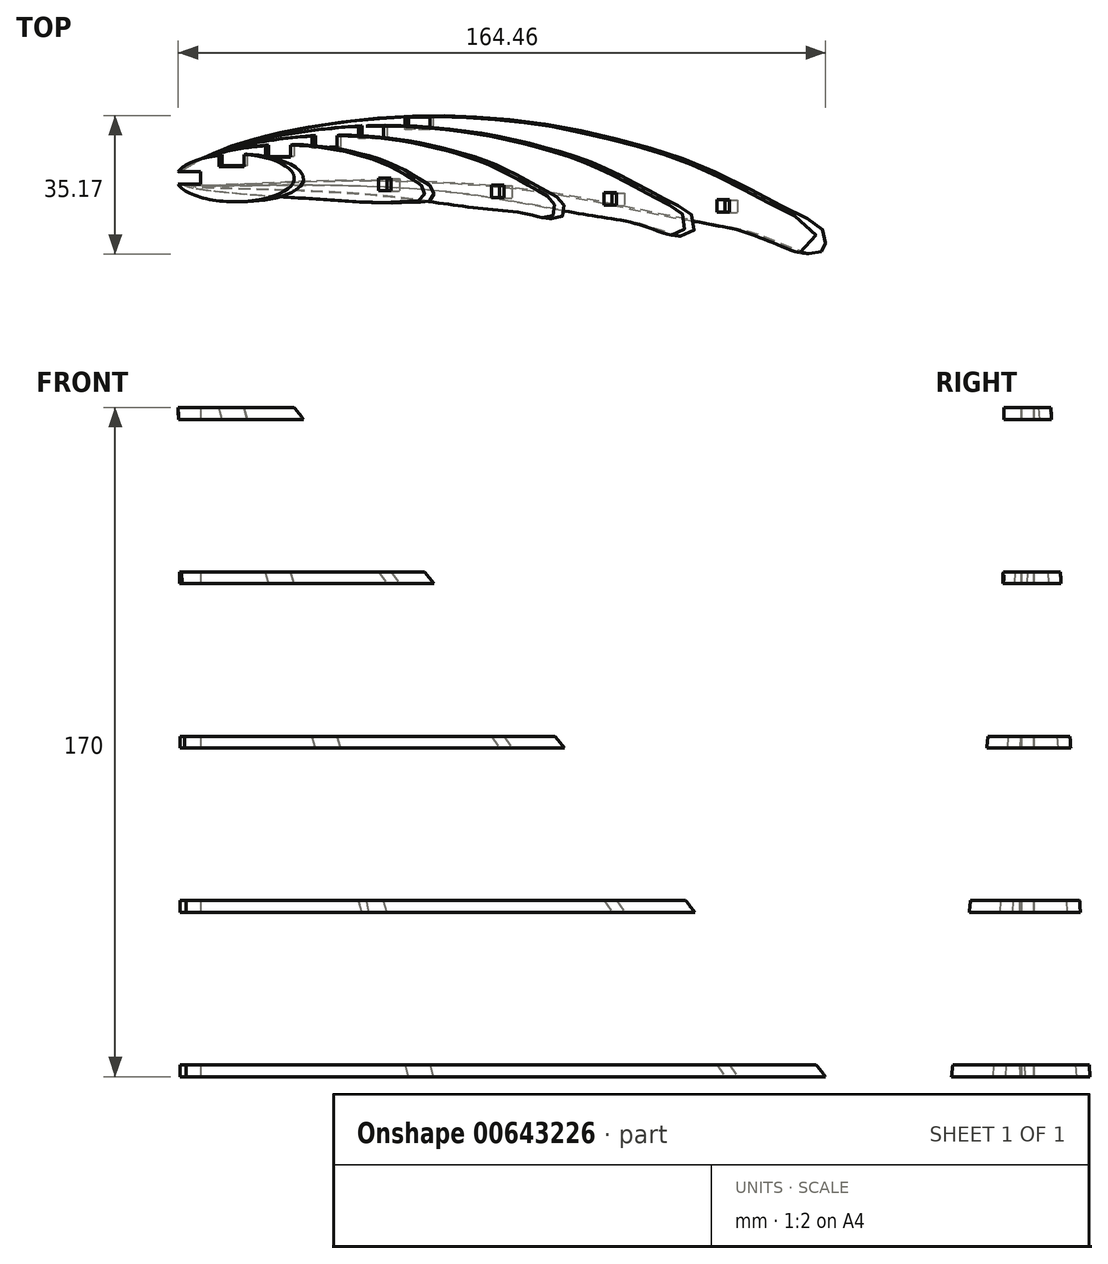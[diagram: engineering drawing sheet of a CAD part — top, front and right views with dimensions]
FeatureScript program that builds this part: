
annotation { "Feature Type Name" : "Feature", "Feature Type Description" : "" }
export const myFeature = defineFeature(function(context is Context, id is Id, definition is map)
    precondition{}
    {
        {
            var Q0;
            Q0=qCreatedBy(makeId("Top.planeOp"),FACE);
            var sketch = newSketch(context, id + "F0", { "sketchPlane" : qUnion([Q0])});
            skLineSegment(sketch, "E0", {"start": v(1, 1.71) * mm, "end": v(3.22, 2.99) * mm});
            skLineSegment(sketch, "E1", {"start": v(3.22, 2.99) * mm, "end": v(5.44, 4.24) * mm});
            skLineSegment(sketch, "E2", {"start": v(5.44, 4.24) * mm, "end": v(7.68, 5.43) * mm});
            skLineSegment(sketch, "E3", {"start": v(7.68, 5.43) * mm, "end": v(9.99, 6.53) * mm});
            skLineSegment(sketch, "E4", {"start": v(9.99, 6.53) * mm, "end": v(12.3, 7.5) * mm});
            skLineSegment(sketch, "E5", {"start": v(12.3, 7.5) * mm, "end": v(14.68, 8.38) * mm});
            skLineSegment(sketch, "E6", {"start": v(14.68, 8.38) * mm, "end": v(17.1, 9.17) * mm});
            skLineSegment(sketch, "E7", {"start": v(17.1, 9.17) * mm, "end": v(19.55, 9.87) * mm});
            skLineSegment(sketch, "E8", {"start": v(19.55, 9.87) * mm, "end": v(22.03, 10.5) * mm});
            skLineSegment(sketch, "E9", {"start": v(22.03, 10.5) * mm, "end": v(26.45, 11.52) * mm});
            skLineSegment(sketch, "E10", {"start": v(26.45, 11.52) * mm, "end": v(29.5, 12.16) * mm});
            skLineSegment(sketch, "E11", {"start": v(29.5, 12.16) * mm, "end": v(34.51, 13.11) * mm});
            skLineSegment(sketch, "E12", {"start": v(34.51, 13.11) * mm, "end": v(37.02, 13.54) * mm});
            skLineSegment(sketch, "E13", {"start": v(37.02, 13.54) * mm, "end": v(39.53, 13.94) * mm});
            skLineSegment(sketch, "E14", {"start": v(39.53, 13.94) * mm, "end": v(42.04, 14.3) * mm});
            skLineSegment(sketch, "E15", {"start": v(42.04, 14.3) * mm, "end": v(44.56, 14.62) * mm});
            skLineSegment(sketch, "E16", {"start": v(44.56, 14.62) * mm, "end": v(48.06, 15.01) * mm});
            skLineSegment(sketch, "E17", {"start": v(48.06, 15.01) * mm, "end": v(49.61, 15.16) * mm});
            skLineSegment(sketch, "E18", {"start": v(49.61, 15.16) * mm, "end": v(52.14, 15.37) * mm});
            skLineSegment(sketch, "E19", {"start": v(52.14, 15.37) * mm, "end": v(54.68, 15.53) * mm});
            skLineSegment(sketch, "E20", {"start": v(54.68, 15.53) * mm, "end": v(57.22, 15.66) * mm});
            skLineSegment(sketch, "E21", {"start": v(57.22, 15.66) * mm, "end": v(59.76, 15.76) * mm});
            skLineSegment(sketch, "E22", {"start": v(59.76, 15.76) * mm, "end": v(62.3, 15.81) * mm});
            skLineSegment(sketch, "E23", {"start": v(62.3, 15.81) * mm, "end": v(64.85, 15.83) * mm});
            skLineSegment(sketch, "E24", {"start": v(64.85, 15.83) * mm, "end": v(67.4, 15.82) * mm});
            skLineSegment(sketch, "E25", {"start": v(67.4, 15.82) * mm, "end": v(69.95, 15.77) * mm});
            skLineSegment(sketch, "E26", {"start": v(69.95, 15.77) * mm, "end": v(72.67, 15.68) * mm});
            skLineSegment(sketch, "E27", {"start": v(72.67, 15.68) * mm, "end": v(75.03, 15.57) * mm});
            skLineSegment(sketch, "E28", {"start": v(75.03, 15.57) * mm, "end": v(77.57, 15.42) * mm});
            skLineSegment(sketch, "E29", {"start": v(77.57, 15.42) * mm, "end": v(80.11, 15.23) * mm});
            skLineSegment(sketch, "E30", {"start": v(80.11, 15.23) * mm, "end": v(82.65, 15.02) * mm});
            skLineSegment(sketch, "E31", {"start": v(82.65, 15.02) * mm, "end": v(85.18, 14.77) * mm});
            skLineSegment(sketch, "E32", {"start": v(85.18, 14.77) * mm, "end": v(87.7, 14.49) * mm});
            skLineSegment(sketch, "E33", {"start": v(87.7, 14.49) * mm, "end": v(90.23, 14.17) * mm});
            skLineSegment(sketch, "E34", {"start": v(90.23, 14.17) * mm, "end": v(92.75, 13.82) * mm});
            skLineSegment(sketch, "E35", {"start": v(92.75, 13.82) * mm, "end": v(95.26, 13.44) * mm});
            skLineSegment(sketch, "E36", {"start": v(95.26, 13.44) * mm, "end": v(97.77, 13.02) * mm});
            skLineSegment(sketch, "E37", {"start": v(97.77, 13.02) * mm, "end": v(100.27, 12.56) * mm});
            skLineSegment(sketch, "E38", {"start": v(100.27, 12.56) * mm, "end": v(102.77, 12.08) * mm});
            skLineSegment(sketch, "E39", {"start": v(102.77, 12.08) * mm, "end": v(105.26, 11.56) * mm});
            skLineSegment(sketch, "E40", {"start": v(105.26, 11.56) * mm, "end": v(107.74, 11) * mm});
            skLineSegment(sketch, "E41", {"start": v(107.74, 11) * mm, "end": v(110.22, 10.41) * mm});
            skLineSegment(sketch, "E42", {"start": v(110.22, 10.41) * mm, "end": v(112.68, 9.79) * mm});
            skLineSegment(sketch, "E43", {"start": v(112.68, 9.79) * mm, "end": v(115.14, 9.13) * mm});
            skLineSegment(sketch, "E44", {"start": v(115.14, 9.13) * mm, "end": v(117.6, 8.44) * mm});
            skLineSegment(sketch, "E45", {"start": v(117.6, 8.44) * mm, "end": v(120.03, 7.72) * mm});
            skLineSegment(sketch, "E46", {"start": v(120.03, 7.72) * mm, "end": v(121.72, 7.2) * mm});
            skLineSegment(sketch, "E47", {"start": v(121.72, 7.2) * mm, "end": v(124.88, 6.17) * mm});
            skLineSegment(sketch, "E48", {"start": v(124.88, 6.17) * mm, "end": v(127.29, 5.34) * mm});
            skLineSegment(sketch, "E49", {"start": v(127.29, 5.34) * mm, "end": v(129.68, 4.48) * mm});
            skLineSegment(sketch, "E50", {"start": v(129.68, 4.48) * mm, "end": v(132.06, 3.58) * mm});
            skLineSegment(sketch, "E51", {"start": v(132.06, 3.58) * mm, "end": v(134.43, 2.64) * mm});
            skLineSegment(sketch, "E52", {"start": v(134.43, 2.64) * mm, "end": v(136.78, 1.66) * mm});
            skLineSegment(sketch, "E53", {"start": v(136.78, 1.66) * mm, "end": v(139.1, 0.64) * mm});
            skLineSegment(sketch, "E54", {"start": v(139.1, 0.64) * mm, "end": v(142.17, -0.78) * mm});
            skLineSegment(sketch, "E55", {"start": v(142.17, -0.78) * mm, "end": v(143.7, -1.53) * mm});
            skLineSegment(sketch, "E56", {"start": v(143.7, -1.53) * mm, "end": v(145.97, -2.68) * mm});
            skLineSegment(sketch, "E57", {"start": v(145.97, -2.68) * mm, "end": v(148.22, -3.85) * mm});
            skLineSegment(sketch, "E58", {"start": v(148.22, -3.85) * mm, "end": v(152.69, -6.28) * mm});
            skLineSegment(sketch, "E59", {"start": v(152.69, -6.28) * mm, "end": v(157.13, -8.76) * mm});
            skLineSegment(sketch, "E60", {"start": v(1, 1.71) * mm, "end": v(0.87, 1.54) * mm});
            skLineSegment(sketch, "E61", {"start": v(0.87, 1.54) * mm, "end": v(0.73, 1.38) * mm});
            skLineSegment(sketch, "E62", {"start": v(0.73, 1.38) * mm, "end": v(0.6, 1.21) * mm});
            skLineSegment(sketch, "E63", {"start": v(0.6, 1.21) * mm, "end": v(0.48, 1.05) * mm});
            skLineSegment(sketch, "E64", {"start": v(0.48, 1.05) * mm, "end": v(0.42, 0.97) * mm});
            skLineSegment(sketch, "E65", {"start": v(0.42, 0.97) * mm, "end": v(0.37, 0.9) * mm});
            skLineSegment(sketch, "E66", {"start": v(0.37, 0.9) * mm, "end": v(0.33, 0.84) * mm});
            skLineSegment(sketch, "E67", {"start": v(0.33, 0.84) * mm, "end": v(0.27, 0.74) * mm});
            skLineSegment(sketch, "E68", {"start": v(0.27, 0.74) * mm, "end": v(0.23, 0.67) * mm});
            skLineSegment(sketch, "E69", {"start": v(0.23, 0.67) * mm, "end": v(0.19, 0.6) * mm});
            skLineSegment(sketch, "E70", {"start": v(0.19, 0.6) * mm, "end": v(0.15, 0.52) * mm});
            skLineSegment(sketch, "E71", {"start": v(0.15, 0.52) * mm, "end": v(0.12, 0.45) * mm});
            skLineSegment(sketch, "E72", {"start": v(0.12, 0.45) * mm, "end": v(0.1, 0.38) * mm});
            skLineSegment(sketch, "E73", {"start": v(0.1, 0.38) * mm, "end": v(0.07, 0.32) * mm});
            skLineSegment(sketch, "E74", {"start": v(0.07, 0.32) * mm, "end": v(0.05, 0.25) * mm});
            skLineSegment(sketch, "E75", {"start": v(0.05, 0.25) * mm, "end": v(0.03, 0.19) * mm});
            skLineSegment(sketch, "E76", {"start": v(0.03, 0.19) * mm, "end": v(0.02, 0.12) * mm});
            skLineSegment(sketch, "E77", {"start": v(0.02, 0.12) * mm, "end": v(0, 0.06) * mm});
            skLineSegment(sketch, "E78", {"start": v(0, 0.06) * mm, "end": v(0, 0) * mm});
            skLineSegment(sketch, "E79", {"start": v(0, 0) * mm, "end": v(0, -0.06) * mm});
            skLineSegment(sketch, "E80", {"start": v(0, -0.06) * mm, "end": v(0, -0.12) * mm});
            skLineSegment(sketch, "E81", {"start": v(0, -0.12) * mm, "end": v(0, -0.18) * mm});
            skLineSegment(sketch, "E82", {"start": v(0, -0.18) * mm, "end": v(0, -0.23) * mm});
            skLineSegment(sketch, "E83", {"start": v(0, -0.23) * mm, "end": v(0.02, -0.29) * mm});
            skLineSegment(sketch, "E84", {"start": v(0.02, -0.29) * mm, "end": v(0.03, -0.34) * mm});
            skLineSegment(sketch, "E85", {"start": v(0.03, -0.34) * mm, "end": v(0.05, -0.4) * mm});
            skLineSegment(sketch, "E86", {"start": v(0.05, -0.4) * mm, "end": v(0.07, -0.44) * mm});
            skLineSegment(sketch, "E87", {"start": v(0.07, -0.44) * mm, "end": v(0.1, -0.5) * mm});
            skLineSegment(sketch, "E88", {"start": v(0.1, -0.5) * mm, "end": v(0.12, -0.54) * mm});
            skLineSegment(sketch, "E89", {"start": v(0.12, -0.54) * mm, "end": v(0.15, -0.6) * mm});
            skLineSegment(sketch, "E90", {"start": v(0.15, -0.6) * mm, "end": v(0.18, -0.64) * mm});
            skLineSegment(sketch, "E91", {"start": v(0.18, -0.64) * mm, "end": v(0.22, -0.68) * mm});
            skLineSegment(sketch, "E92", {"start": v(0.22, -0.68) * mm, "end": v(0.25, -0.73) * mm});
            skLineSegment(sketch, "E93", {"start": v(0.25, -0.73) * mm, "end": v(0.3, -0.77) * mm});
            skLineSegment(sketch, "E94", {"start": v(0.3, -0.77) * mm, "end": v(0.34, -0.81) * mm});
            skLineSegment(sketch, "E95", {"start": v(0.34, -0.81) * mm, "end": v(0.39, -0.86) * mm});
            skLineSegment(sketch, "E96", {"start": v(0.39, -0.86) * mm, "end": v(0.44, -0.9) * mm});
            skLineSegment(sketch, "E97", {"start": v(0.44, -0.9) * mm, "end": v(0.5, -0.94) * mm});
            skLineSegment(sketch, "E98", {"start": v(0.5, -0.94) * mm, "end": v(0.6, -1.01) * mm});
            skLineSegment(sketch, "E99", {"start": v(0.6, -1.01) * mm, "end": v(0.73, -1.08) * mm});
            skLineSegment(sketch, "E100", {"start": v(0.73, -1.08) * mm, "end": v(0.87, -1.15) * mm});
            skLineSegment(sketch, "E101", {"start": v(0.87, -1.15) * mm, "end": v(1.02, -1.22) * mm});
            skLineSegment(sketch, "E102", {"start": v(1.02, -1.22) * mm, "end": v(1.17, -1.28) * mm});
            skLineSegment(sketch, "E103", {"start": v(1.17, -1.28) * mm, "end": v(1.34, -1.33) * mm});
            skLineSegment(sketch, "E104", {"start": v(1.34, -1.33) * mm, "end": v(1.52, -1.39) * mm});
            skLineSegment(sketch, "E105", {"start": v(1.52, -1.39) * mm, "end": v(1.7, -1.44) * mm});
            skLineSegment(sketch, "E106", {"start": v(1.7, -1.44) * mm, "end": v(1.9, -1.48) * mm});
            skLineSegment(sketch, "E107", {"start": v(1.9, -1.48) * mm, "end": v(2.1, -1.53) * mm});
            skLineSegment(sketch, "E108", {"start": v(2.1, -1.53) * mm, "end": v(2.32, -1.57) * mm});
            skLineSegment(sketch, "E109", {"start": v(2.32, -1.57) * mm, "end": v(2.54, -1.6) * mm});
            skLineSegment(sketch, "E110", {"start": v(2.54, -1.6) * mm, "end": v(2.77, -1.64) * mm});
            skLineSegment(sketch, "E111", {"start": v(2.77, -1.64) * mm, "end": v(3, -1.67) * mm});
            skLineSegment(sketch, "E112", {"start": v(3, -1.67) * mm, "end": v(3.25, -1.7) * mm});
            skLineSegment(sketch, "E113", {"start": v(3.25, -1.7) * mm, "end": v(3.5, -1.73) * mm});
            skLineSegment(sketch, "E114", {"start": v(3.5, -1.73) * mm, "end": v(3.77, -1.75) * mm});
            skLineSegment(sketch, "E115", {"start": v(3.77, -1.75) * mm, "end": v(4.03, -1.77) * mm});
            skLineSegment(sketch, "E116", {"start": v(4.03, -1.77) * mm, "end": v(4.3, -1.8) * mm});
            skLineSegment(sketch, "E117", {"start": v(4.3, -1.8) * mm, "end": v(4.59, -1.8) * mm});
            skLineSegment(sketch, "E118", {"start": v(4.59, -1.8) * mm, "end": v(4.87, -1.82) * mm});
            skLineSegment(sketch, "E119", {"start": v(4.87, -1.82) * mm, "end": v(5.16, -1.83) * mm});
            skLineSegment(sketch, "E120", {"start": v(5.16, -1.83) * mm, "end": v(5.46, -1.84) * mm});
            skLineSegment(sketch, "E121", {"start": v(5.46, -1.84) * mm, "end": v(5.76, -1.85) * mm});
            skLineSegment(sketch, "E122", {"start": v(5.76, -1.85) * mm, "end": v(6.07, -1.86) * mm});
            skLineSegment(sketch, "E123", {"start": v(6.07, -1.86) * mm, "end": v(6.38, -1.86) * mm});
            skLineSegment(sketch, "E124", {"start": v(6.38, -1.86) * mm, "end": v(6.7, -1.87) * mm});
            skLineSegment(sketch, "E125", {"start": v(6.7, -1.87) * mm, "end": v(7.02, -1.87) * mm});
            skLineSegment(sketch, "E126", {"start": v(7.02, -1.87) * mm, "end": v(7.34, -1.87) * mm});
            skLineSegment(sketch, "E127", {"start": v(7.34, -1.87) * mm, "end": v(7.67, -1.87) * mm});
            skLineSegment(sketch, "E128", {"start": v(7.67, -1.87) * mm, "end": v(8, -1.87) * mm});
            skLineSegment(sketch, "E129", {"start": v(8, -1.87) * mm, "end": v(8.34, -1.86) * mm});
            skLineSegment(sketch, "E130", {"start": v(8.34, -1.86) * mm, "end": v(8.67, -1.86) * mm});
            skLineSegment(sketch, "E131", {"start": v(8.67, -1.86) * mm, "end": v(9.36, -1.85) * mm});
            skLineSegment(sketch, "E132", {"start": v(9.36, -1.85) * mm, "end": v(10.05, -1.83) * mm});
            skLineSegment(sketch, "E133", {"start": v(10.05, -1.83) * mm, "end": v(10.74, -1.82) * mm});
            skLineSegment(sketch, "E134", {"start": v(10.74, -1.82) * mm, "end": v(12.15, -1.78) * mm});
            skLineSegment(sketch, "E135", {"start": v(157.13, -8.76) * mm, "end": v(159.65, -9.9) * mm});
            skLineSegment(sketch, "E136", {"start": v(159.65, -9.9) * mm, "end": v(162.12, -11.02) * mm});
            skLineSegment(sketch, "E137", {"start": v(162.12, -11.02) * mm, "end": v(163.97, -12.8) * mm});
            skLineSegment(sketch, "E138", {"start": v(163.97, -12.8) * mm, "end": v(165.18, -13.97) * mm});
            skLineSegment(sketch, "E139", {"start": v(165.18, -13.97) * mm, "end": v(165.11, -15.41) * mm});
            skLineSegment(sketch, "E140", {"start": v(165.11, -15.41) * mm, "end": v(164.85, -16.72) * mm});
            skLineSegment(sketch, "E141", {"start": v(164.85, -16.72) * mm, "end": v(164.68, -17.32) * mm});
            skLineSegment(sketch, "E142", {"start": v(164.68, -17.32) * mm, "end": v(164.48, -17.86) * mm});
            skLineSegment(sketch, "E143", {"start": v(164.48, -17.86) * mm, "end": v(164.28, -18.24) * mm});
            skLineSegment(sketch, "E144", {"start": v(164.28, -18.24) * mm, "end": v(163.92, -18.7) * mm});
            skLineSegment(sketch, "E145", {"start": v(163.92, -18.7) * mm, "end": v(163.55, -18.98) * mm});
            skLineSegment(sketch, "E146", {"start": v(163.55, -18.98) * mm, "end": v(163.13, -19.18) * mm});
            skLineSegment(sketch, "E147", {"start": v(163.13, -19.18) * mm, "end": v(162.66, -19.3) * mm});
            skLineSegment(sketch, "E148", {"start": v(162.66, -19.3) * mm, "end": v(162.15, -19.36) * mm});
            skLineSegment(sketch, "E149", {"start": v(162.15, -19.36) * mm, "end": v(161.6, -19.35) * mm});
            skLineSegment(sketch, "E150", {"start": v(161.6, -19.35) * mm, "end": v(161, -19.28) * mm});
            skLineSegment(sketch, "E151", {"start": v(161, -19.28) * mm, "end": v(160.39, -19.16) * mm});
            skLineSegment(sketch, "E152", {"start": v(160.39, -19.16) * mm, "end": v(159.74, -19) * mm});
            skLineSegment(sketch, "E153", {"start": v(159.74, -19) * mm, "end": v(159.07, -18.79) * mm});
            skLineSegment(sketch, "E154", {"start": v(159.07, -18.79) * mm, "end": v(158.37, -18.54) * mm});
            skLineSegment(sketch, "E155", {"start": v(158.37, -18.54) * mm, "end": v(156.94, -17.98) * mm});
            skLineSegment(sketch, "E156", {"start": v(156.94, -17.98) * mm, "end": v(155.48, -17.36) * mm});
            skLineSegment(sketch, "E157", {"start": v(155.48, -17.36) * mm, "end": v(153.3, -16.41) * mm});
            skLineSegment(sketch, "E158", {"start": v(153.3, -16.41) * mm, "end": v(152.58, -16.1) * mm});
            skLineSegment(sketch, "E159", {"start": v(152.58, -16.1) * mm, "end": v(151.19, -15.54) * mm});
            skLineSegment(sketch, "E160", {"start": v(151.19, -15.54) * mm, "end": v(149.84, -15.03) * mm});
            skLineSegment(sketch, "E161", {"start": v(149.84, -15.03) * mm, "end": v(148.53, -14.57) * mm});
            skLineSegment(sketch, "E162", {"start": v(148.53, -14.57) * mm, "end": v(147.26, -14.14) * mm});
            skLineSegment(sketch, "E163", {"start": v(147.26, -14.14) * mm, "end": v(146.02, -13.76) * mm});
            skLineSegment(sketch, "E164", {"start": v(146.02, -13.76) * mm, "end": v(144.8, -13.4) * mm});
            skLineSegment(sketch, "E165", {"start": v(144.8, -13.4) * mm, "end": v(143.62, -13.09) * mm});
            skLineSegment(sketch, "E166", {"start": v(143.62, -13.09) * mm, "end": v(142.46, -12.8) * mm});
            skLineSegment(sketch, "E167", {"start": v(142.46, -12.8) * mm, "end": v(140.2, -12.3) * mm});
            skLineSegment(sketch, "E168", {"start": v(140.2, -12.3) * mm, "end": v(137.98, -11.85) * mm});
            skLineSegment(sketch, "E169", {"start": v(137.98, -11.85) * mm, "end": v(133.6, -11.09) * mm});
            skLineSegment(sketch, "E170", {"start": v(133.6, -11.09) * mm, "end": v(131.7, -10.76) * mm});
            skLineSegment(sketch, "E171", {"start": v(131.7, -10.76) * mm, "end": v(129.14, -10.3) * mm});
            skLineSegment(sketch, "E172", {"start": v(129.14, -10.3) * mm, "end": v(126.85, -9.85) * mm});
            skLineSegment(sketch, "E173", {"start": v(126.85, -9.85) * mm, "end": v(124.52, -9.39) * mm});
            skLineSegment(sketch, "E174", {"start": v(124.52, -9.39) * mm, "end": v(122.15, -8.9) * mm});
            skLineSegment(sketch, "E175", {"start": v(122.15, -8.9) * mm, "end": v(119.76, -8.4) * mm});
            skLineSegment(sketch, "E176", {"start": v(119.76, -8.4) * mm, "end": v(114.91, -7.38) * mm});
            skLineSegment(sketch, "E177", {"start": v(114.91, -7.38) * mm, "end": v(110, -6.37) * mm});
            skLineSegment(sketch, "E178", {"start": v(110, -6.37) * mm, "end": v(105.06, -5.4) * mm});
            skLineSegment(sketch, "E179", {"start": v(105.06, -5.4) * mm, "end": v(100.77, -4.6) * mm});
            skLineSegment(sketch, "E180", {"start": v(100.77, -4.6) * mm, "end": v(95.2, -3.7) * mm});
            skLineSegment(sketch, "E181", {"start": v(95.2, -3.7) * mm, "end": v(90.32, -3.02) * mm});
            skLineSegment(sketch, "E182", {"start": v(90.32, -3.02) * mm, "end": v(85.45, -2.43) * mm});
            skLineSegment(sketch, "E183", {"start": v(85.45, -2.43) * mm, "end": v(80.6, -1.94) * mm});
            skLineSegment(sketch, "E184", {"start": v(80.6, -1.94) * mm, "end": v(75.74, -1.53) * mm});
            skLineSegment(sketch, "E185", {"start": v(75.74, -1.53) * mm, "end": v(70.88, -1.2) * mm});
            skLineSegment(sketch, "E186", {"start": v(70.88, -1.2) * mm, "end": v(66.02, -0.95) * mm});
            skLineSegment(sketch, "E187", {"start": v(66.02, -0.95) * mm, "end": v(61.14, -0.76) * mm});
            skLineSegment(sketch, "E188", {"start": v(61.14, -0.76) * mm, "end": v(56.25, -0.64) * mm});
            skLineSegment(sketch, "E189", {"start": v(56.25, -0.64) * mm, "end": v(51.35, -0.58) * mm});
            skLineSegment(sketch, "E190", {"start": v(51.35, -0.58) * mm, "end": v(46.44, -0.58) * mm});
            skLineSegment(sketch, "E191", {"start": v(46.44, -0.58) * mm, "end": v(41.53, -0.63) * mm});
            skLineSegment(sketch, "E192", {"start": v(41.53, -0.63) * mm, "end": v(34.6, -0.78) * mm});
            skLineSegment(sketch, "E193", {"start": v(34.6, -0.78) * mm, "end": v(31.72, -0.88) * mm});
            skLineSegment(sketch, "E194", {"start": v(31.72, -0.88) * mm, "end": v(21.93, -1.29) * mm});
            skLineSegment(sketch, "E195", {"start": v(21.93, -1.29) * mm, "end": v(12.15, -1.78) * mm});
            skSolve(sketch);
        }
        {
            var Q0;
            Q0=qCreatedBy(makeId("Top.planeOp"),FACE);
            var sketch = newSketch(context, id + "F1", { "sketchPlane" : qUnion([Q0])});
            skPoint(sketch, "E196.0", {"position": v(0, 0) * mm});
            skPoint(sketch, "E196.1", {"position": v(0.1, 0.38) * mm});
            skPoint(sketch, "E196.2", {"position": v(0.33, 0.84) * mm});
            skPoint(sketch, "E196.3", {"position": v(0.73, 1.38) * mm});
            skPoint(sketch, "E196.4", {"position": v(5.44, 4.24) * mm});
            skPoint(sketch, "E196.5", {"position": v(12.3, 7.5) * mm});
            skPoint(sketch, "E196.6", {"position": v(22.03, 10.5) * mm});
            skPoint(sketch, "E196.7", {"position": v(57.22, 15.66) * mm});
            skPoint(sketch, "E196.8", {"position": v(75.03, 15.57) * mm});
            skPoint(sketch, "E196.9", {"position": v(95.26, 13.44) * mm});
            skPoint(sketch, "E196.10", {"position": v(117.6, 8.44) * mm});
            skPoint(sketch, "E196.11", {"position": v(136.78, 1.66) * mm});
            skPoint(sketch, "E196.12", {"position": v(157.13, -8.76) * mm});
            skPoint(sketch, "E196.13", {"position": v(163.97, -12.8) * mm});
            skPoint(sketch, "E196.14", {"position": v(164.48, -17.86) * mm});
            skPoint(sketch, "E196.15", {"position": v(163.55, -18.98) * mm});
            skPoint(sketch, "E196.16", {"position": v(160.39, -19.16) * mm});
            skPoint(sketch, "E196.17", {"position": v(155.48, -17.36) * mm});
            skPoint(sketch, "E196.18", {"position": v(148.53, -14.57) * mm});
            skPoint(sketch, "E196.19", {"position": v(143.62, -13.09) * mm});
            skPoint(sketch, "E196.20", {"position": v(105.06, -5.4) * mm});
            skPoint(sketch, "E196.21", {"position": v(80.6, -1.94) * mm});
            skPoint(sketch, "E196.22", {"position": v(51.35, -0.58) * mm});
            skPoint(sketch, "E196.23", {"position": v(21.93, -1.29) * mm});
            skPoint(sketch, "E196.24", {"position": v(9.36, -1.85) * mm});
            skPoint(sketch, "E196.25", {"position": v(5.46, -1.84) * mm});
            skPoint(sketch, "E196.26", {"position": v(3, -1.67) * mm});
            skPoint(sketch, "E196.27", {"position": v(0.39, -0.86) * mm});
            skPoint(sketch, "E196.28", {"position": v(0.1, -0.5) * mm});
            skPoint(sketch, "E196.29", {"position": v(35.77, 13.33) * mm});
            skPoint(sketch, "E196.30", {"position": v(164.98, -16.07) * mm});
            skPoint(sketch, "E196.31", {"position": v(125.68, -9.62) * mm});
            skPoint(sketch, "E196.32", {"position": v(38.06, -0.7) * mm});
            skFitSpline(sketch, "E197", {"points": [v(0, 0) * mm, v(0.1, 0.38) * mm, v(0.33, 0.84) * mm, v(0.73, 1.38) * mm, v(5.44, 4.24) * mm, v(12.3, 7.5) * mm, v(22.03, 10.5) * mm, v(35.77, 13.33) * mm, v(57.22, 15.66) * mm, v(75.03, 15.57) * mm, v(95.26, 13.44) * mm, v(117.6, 8.44) * mm, v(136.78, 1.66) * mm, v(157.13, -8.76) * mm, v(163.97, -12.8) * mm, v(164.98, -16.07) * mm, v(164.48, -17.86) * mm, v(163.55, -18.98) * mm, v(160.39, -19.16) * mm, v(155.48, -17.36) * mm, v(148.53, -14.57) * mm, v(143.62, -13.09) * mm, v(125.68, -9.62) * mm, v(105.06, -5.4) * mm, v(80.6, -1.94) * mm, v(51.35, -0.58) * mm, v(38.06, -0.7) * mm, v(21.93, -1.29) * mm, v(9.36, -1.85) * mm, v(5.46, -1.84) * mm, v(3, -1.67) * mm, v(0.39, -0.86) * mm, v(0.1, -0.5) * mm, v(0, 0) * mm]});
            skSolve(sketch);
        }
        {
            var Q0;
            Q0=qCreatedBy(makeId("Top.planeOp"),FACE);
            cPlane(context, id + "F2", {"entities" : qUnion([Q0]), "cplaneType" : CPlaneType.OFFSET, "offset" : 170 * mm, "width" : 150 * mm, "height" : 150 * mm});
        }
        {
            var Q0;
            Q0=qCreatedBy(id+"F2.planeOp",FACE);
            var sketch = newSketch(context, id + "F3", { "sketchPlane" : qUnion([Q0])});
            skEllipse(sketch, "E198", {"center": v(15, 0) * mm, "majorRadius": 15 * mm, "minorRadius": 6.01 * mm, "majorAxis": v(-1, 0)});
            skSolve(sketch);
        }
        {
            var Q0;
            Q0=makeQuery(id+"F1.imprint","IMPRINT",FACE,{"disambiguationData":[TD([[makeQuery(id+"F1.imprint","IMPRINT",EDGE,{"derivedFrom":sQuery(id+"F1.wireOp",EDGE,"E197")}),-1.0]])]});
            var Q1;
            Q1=makeQuery(id+"F3.imprint","IMPRINT",FACE,{"disambiguationData":[TD([[makeQuery(id+"F3.imprint","IMPRINT",EDGE,{"derivedFrom":sQuery(id+"F3.wireOp",EDGE,"E198")}),1.0]])]});
            loft(context, id + "F4", {"sheetProfilesArray" : [{ "sheetProfileEntities" : qUnion([Q0]) }, { "sheetProfileEntities" : qUnion([Q1]) }]});
        }
        {
            var Q0;
            Q0=qCreatedBy(makeId("Front.planeOp"),FACE);
            var sketch = newSketch(context, id + "F5", { "sketchPlane" : qUnion([Q0])});
            skLineSegment(sketch, "E199", {"start": v(0, 0) * mm, "end": v(0, 3) * mm, "construction": true});
            skLineSegment(sketch, "E200.bottom", {"start": v(0, 3) * mm, "end": v(214.07, 3) * mm});
            skLineSegment(sketch, "E200.top", {"start": v(0, 41.75) * mm, "end": v(214.07, 41.75) * mm});
            skLineSegment(sketch, "E200.left", {"start": v(0, 3) * mm, "end": v(0, 41.75) * mm});
            skLineSegment(sketch, "E200.right", {"start": v(214.07, 3) * mm, "end": v(214.07, 41.75) * mm});
            skLineSegment(sketch, "E201", {"start": v(0, 41.75) * mm, "end": v(0, 44.75) * mm, "construction": true});
            skLineSegment(sketch, "E202.0.1.0", {"start": v(0, 83.5) * mm, "end": v(214.07, 83.5) * mm});
            skLineSegment(sketch, "E202.0.1.1", {"start": v(0, 44.75) * mm, "end": v(0, 83.5) * mm});
            skLineSegment(sketch, "E202.0.1.2", {"start": v(214.07, 44.75) * mm, "end": v(214.07, 83.5) * mm});
            skLineSegment(sketch, "E202.0.1.3", {"start": v(0, 44.75) * mm, "end": v(214.07, 44.75) * mm});
            skLineSegment(sketch, "E202.0.1.4", {"start": v(0, 83.5) * mm, "end": v(0, 86.5) * mm, "construction": true});
            skLineSegment(sketch, "E202.0.2.0", {"start": v(0, 125.25) * mm, "end": v(214.07, 125.25) * mm});
            skLineSegment(sketch, "E202.0.2.1", {"start": v(0, 86.5) * mm, "end": v(0, 125.25) * mm});
            skLineSegment(sketch, "E202.0.2.2", {"start": v(214.07, 86.5) * mm, "end": v(214.07, 125.25) * mm});
            skLineSegment(sketch, "E202.0.2.3", {"start": v(0, 86.5) * mm, "end": v(214.07, 86.5) * mm});
            skLineSegment(sketch, "E202.0.2.4", {"start": v(0, 125.25) * mm, "end": v(0, 128.25) * mm, "construction": true});
            skLineSegment(sketch, "E202.0.2.5", {"start": v(0, 83.5) * mm, "end": v(0, 86.5) * mm, "construction": true});
            skLineSegment(sketch, "E202.0.3.0", {"start": v(0, 167) * mm, "end": v(214.07, 167) * mm});
            skLineSegment(sketch, "E202.0.3.1", {"start": v(0, 128.25) * mm, "end": v(0, 167) * mm});
            skLineSegment(sketch, "E202.0.3.2", {"start": v(214.07, 128.25) * mm, "end": v(214.07, 167) * mm});
            skLineSegment(sketch, "E202.0.3.3", {"start": v(0, 128.25) * mm, "end": v(214.07, 128.25) * mm});
            skLineSegment(sketch, "E202.0.3.4", {"start": v(0, 167) * mm, "end": v(0, 170) * mm, "construction": true});
            skLineSegment(sketch, "E202.0.3.5", {"start": v(0, 125.25) * mm, "end": v(0, 128.25) * mm, "construction": true});
            skLineSegment(sketch, "E202.direction1", {"start": v(0, 0) * mm, "end": v(25, 0) * mm, "construction": true});
            skLineSegment(sketch, "E202.direction2", {"start": v(0, 0) * mm, "end": v(0, 41.75) * mm, "construction": true});
            skSolve(sketch);
        }
        {
            var Q0;
            Q0 = qSketchRegion(id + "F5", true);
            extrude(context, id + "F6", {"entities" : qUnion([Q0]), "operationType" : NewBodyOperationType.REMOVE, "oppositeDirection" : true, "depth" : 25 * mm, "offsetDistance" : 25 * mm});
        }
        {
            var Q0;
            Q0 = qSketchRegion(id + "F5", true);
            extrude(context, id + "F7", {"entities" : qUnion([Q0]), "operationType" : NewBodyOperationType.REMOVE, "depth" : 25 * mm, "offsetDistance" : 25 * mm});
        }
        {
            var Q0;
            Q0=qCreatedBy(makeId("Top.planeOp"),FACE);
            var sketch = newSketch(context, id + "F8", { "sketchPlane" : qUnion([Q0])});
            skLineSegment(sketch, "E203", {"start": v(0, 0) * mm, "end": v(3, 0) * mm, "construction": true});
            skLineSegment(sketch, "E204.bottom", {"start": v(6.17, -1.59) * mm, "end": v(-0.17, -1.59) * mm});
            skLineSegment(sketch, "E204.top", {"start": v(6.17, 1.59) * mm, "end": v(-0.17, 1.59) * mm});
            skLineSegment(sketch, "E204.left", {"start": v(6.17, -1.59) * mm, "end": v(6.17, 1.59) * mm});
            skLineSegment(sketch, "E204.right", {"start": v(-0.17, -1.59) * mm, "end": v(-0.18, 1.59) * mm});
            skPoint(sketch, "E204.middle", {"position": v(3, 0) * mm});
            skSolve(sketch);
        }
        {
            var Q0;
            Q0=makeQuery(id+"F8.imprint","IMPRINT",FACE,{"disambiguationData":[TD([[makeQuery(id+"F8.imprint","IMPRINT",EDGE,{"derivedFrom":sQuery(id+"F8.wireOp",EDGE,"E204.bottom")}),-1.0]])]});
            extrude(context, id + "F9", {"entities" : qUnion([Q0]), "operationType" : NewBodyOperationType.REMOVE, "depth" : 204.2 * mm, "offsetDistance" : 25 * mm});
        }
        {
            var Q0;
            Q0=qCreatedBy(makeId("Top.planeOp"),FACE);
            var sketch = newSketch(context, id + "F10", { "sketchPlane" : qUnion([Q0])});
            skPoint(sketch, "E205", {"position": v(62.22, 15.71) * mm});
            skLineSegment(sketch, "E206", {"start": v(62.22, 15.71) * mm, "end": v(62.22, 12.5) * mm, "construction": true});
            skLineSegment(sketch, "E207", {"start": v(62.22, 12.5) * mm, "end": v(59.05, 12.5) * mm});
            skLineSegment(sketch, "E208", {"start": v(62.22, 12.5) * mm, "end": v(65.4, 12.5) * mm});
            skLineSegment(sketch, "E209", {"start": v(65.4, 12.5) * mm, "end": v(65.4, 15.71) * mm});
            skLineSegment(sketch, "E210", {"start": v(65.4, 15.71) * mm, "end": v(59.05, 15.71) * mm});
            skLineSegment(sketch, "E211", {"start": v(59.05, 15.71) * mm, "end": v(59.05, 12.5) * mm});
            skPoint(sketch, "E212", {"position": v(14.04, 6.12) * mm});
            skLineSegment(sketch, "E213", {"start": v(14.04, 6.12) * mm, "end": v(14.04, 2.95) * mm, "construction": true});
            skLineSegment(sketch, "E214", {"start": v(14.04, 2.95) * mm, "end": v(10.86, 2.95) * mm});
            skLineSegment(sketch, "E215", {"start": v(10.86, 2.95) * mm, "end": v(10.86, 6.12) * mm});
            skLineSegment(sketch, "E216", {"start": v(10.86, 6.12) * mm, "end": v(14.04, 6.12) * mm});
            skLineSegment(sketch, "E217", {"start": v(14.04, 6.12) * mm, "end": v(17.22, 6.12) * mm});
            skLineSegment(sketch, "E218", {"start": v(17.22, 6.12) * mm, "end": v(17.22, 2.95) * mm});
            skLineSegment(sketch, "E219", {"start": v(17.22, 2.95) * mm, "end": v(14.04, 2.95) * mm});
            skSolve(sketch);
        }
        {
            var Q0;
            Q0=makeQuery(id+"F4.opLoft","CAP_FACE",FACE,{"disambiguationData":[OSD([makeQuery(id+"F3.imprint","IMPRINT",FACE,{"disambiguationData":[TD([[makeQuery(id+"F3.imprint","IMPRINT",EDGE,{"derivedFrom":sQuery(id+"F3.wireOp",EDGE,"E198")}),1.0]])]})])],"isStart":true});
            var sketch = newSketch(context, id + "F11", { "sketchPlane" : qUnion([Q0])});
            skLineSegment(sketch, "E220", {"start": v(17.27, 2.94) * mm, "end": v(10.85, 2.94) * mm});
            skLineSegment(sketch, "E221", {"start": v(10.85, 2.94) * mm, "end": v(10.85, 6.1) * mm});
            skLineSegment(sketch, "E222", {"start": v(10.85, 6.1) * mm, "end": v(17.23, 6.1) * mm});
            skLineSegment(sketch, "E223", {"start": v(17.23, 6.1) * mm, "end": v(17.27, 2.94) * mm});
            skSolve(sketch);
        }
        {
            var Q0;
            Q0=sQuery(id+"F11.wireOp",VERTEX,"E221.start");
            var Q1;
            Q1=sQuery(id+"F10.wireOp",VERTEX,"E211.start");
            var Q2;
            Q2=sQuery(id+"F10.wireOp",VERTEX,"E211.end");
            cPlane(context, id + "F12", {"entities" : qUnion([Q0, Q1, Q2]), "cplaneType" : CPlaneType.THREE_POINT, "offset" : 25 * mm, "width" : 150 * mm, "height" : 150 * mm});
        }
        {
            var Q0;
            Q0=qCreatedBy(id+"F12.planeOp",FACE);
            var sketch = newSketch(context, id + "F13", { "sketchPlane" : qUnion([Q0])});
            skPoint(sketch, "E224.0", {"position": v(2.94, 160.6) * mm});
            skPoint(sketch, "E225.0", {"position": v(12.5, -16.1) * mm});
            skLineSegment(sketch, "E226", {"start": v(12.5, -16.1) * mm, "end": v(2.94, 160.6) * mm});
            skSolve(sketch);
        }
        {
            var Q0;
            Q0=makeQuery(id+"F10.imprint","IMPRINT",FACE,{"disambiguationData":[TD([[makeQuery(id+"F10.imprint","IMPRINT",EDGE,{"derivedFrom":sQuery(id+"F10.wireOp",EDGE,"E207")}),-1.0]])]});
            var Q1;
            Q1=sQuery(id+"F13.wireOp",EDGE,"E226");
            sweep(context, id + "F14", {"operationType" : NewBodyOperationType.REMOVE, "profiles" : qUnion([Q0]), "path" : qUnion([Q1])});
        }
        {
            var Q0;
            {var subQ0=sQuery(id+"F5.wireOp",EDGE,"E202.0.3.3");Q0=makeQuery(id+"F7.boolean.opBoolean","MERGE",FACE,{"derivedFrom":[makeQuery(id+"F6.boolean.opBoolean","COPY",FACE,{"derivedFrom":makeQuery(id+"F6.opExtrude","SWEPT_FACE",FACE,{"disambiguationData":[OSD([subQ0])]})}),makeQuery(id+"F7.opExtrude","SWEPT_FACE",FACE,{"disambiguationData":[OSD([subQ0])]})]});}
            var sketch = newSketch(context, id + "F15", { "sketchPlane" : qUnion([Q0])});
            skLineSegment(sketch, "E227.bottom", {"start": v(51.47, 0) * mm, "end": v(54.64, 0) * mm});
            skLineSegment(sketch, "E227.top", {"start": v(51.47, -3.18) * mm, "end": v(54.64, -3.18) * mm});
            skLineSegment(sketch, "E227.left", {"start": v(51.47, 0) * mm, "end": v(51.47, -3.18) * mm});
            skLineSegment(sketch, "E227.right", {"start": v(54.64, 0) * mm, "end": v(54.64, -3.18) * mm});
            skSolve(sketch);
        }
        {
            var Q0;
            Q0=makeQuery(id+"F4.opLoft","CAP_FACE",FACE,{"disambiguationData":[OSD([makeQuery(id+"F1.imprint","IMPRINT",FACE,{"disambiguationData":[TD([[makeQuery(id+"F1.imprint","IMPRINT",EDGE,{"derivedFrom":sQuery(id+"F1.wireOp",EDGE,"E197")}),-1.0]])]})])],"isStart":true});
            var sketch = newSketch(context, id + "F16", { "sketchPlane" : qUnion([Q0])});
            skLineSegment(sketch, "E228.bottom", {"start": v(139.4, 5.64) * mm, "end": v(142.58, 5.64) * mm});
            skLineSegment(sketch, "E228.top", {"start": v(139.4, 8.82) * mm, "end": v(142.58, 8.82) * mm});
            skLineSegment(sketch, "E228.left", {"start": v(139.4, 5.64) * mm, "end": v(139.4, 8.82) * mm});
            skLineSegment(sketch, "E228.right", {"start": v(142.58, 5.64) * mm, "end": v(142.58, 8.82) * mm});
            skPoint(sketch, "E228.middle", {"position": v(141, 7.23) * mm});
            skSolve(sketch);
        }
        {
            var Q0;
            Q0 = qSketchRegion(id + "F15", true);
            var Q1;
            Q1 = qSketchRegion(id + "F16", true);
            loft(context, id + "F17", {"operationType" : NewBodyOperationType.REMOVE, "sheetProfilesArray" : [{ "sheetProfileEntities" : qUnion([Q0]) }, { "sheetProfileEntities" : qUnion([Q1]) }]});
        }
    });
